# Revit family: Lavatory-Metcraft-Security-5680
name_source: partatom
category: Plumbing Fixtures
revit_build: Autodesk Revit MEP 2015 (Build: 20140606_1530(x64)
units: mm (PartAtom-declared; Revit-internal decimal feet)

## types (1)
- Lavatory-Metcraft-Security-5680
    ADA Compliant = Yes
    Assembly Code = D2010310
    CW Connection = Yes
    Cold water connection = .5" Connection In Chase
    Description = Security Lavatory
    Fixture Hyperlink = http://metcraftindustries.com
    Fixture Submittal = http://metcraftindustries.com
    HW Connection = Yes
    Hot water connection = .5" Connection In Chase
    Industry Standards = ASME A112.19.3 / CSA B45.4
    Instalation Type = Wall Mounted / Wall Outlet Waste
    Manufacturer = Metcraft Industries
    Manufacturer URL = http://metcraftindustries.com
    Masterformat Number = 22 46 16. 13
    Masterformat Title = Security Lavatory
    Material = 304 Stainless Steel
    Model = 5680
    Mounting Height = 2' - 10"
    Omniclass Number = 23-31 13 00
    Omniclass Title = Sinks
    Waste Connection = Yes
    Waste Tube = 1.25"

## geometry (parser evidence)
native form markers: Sweep x2
no freeform markers — native parametric forms only
